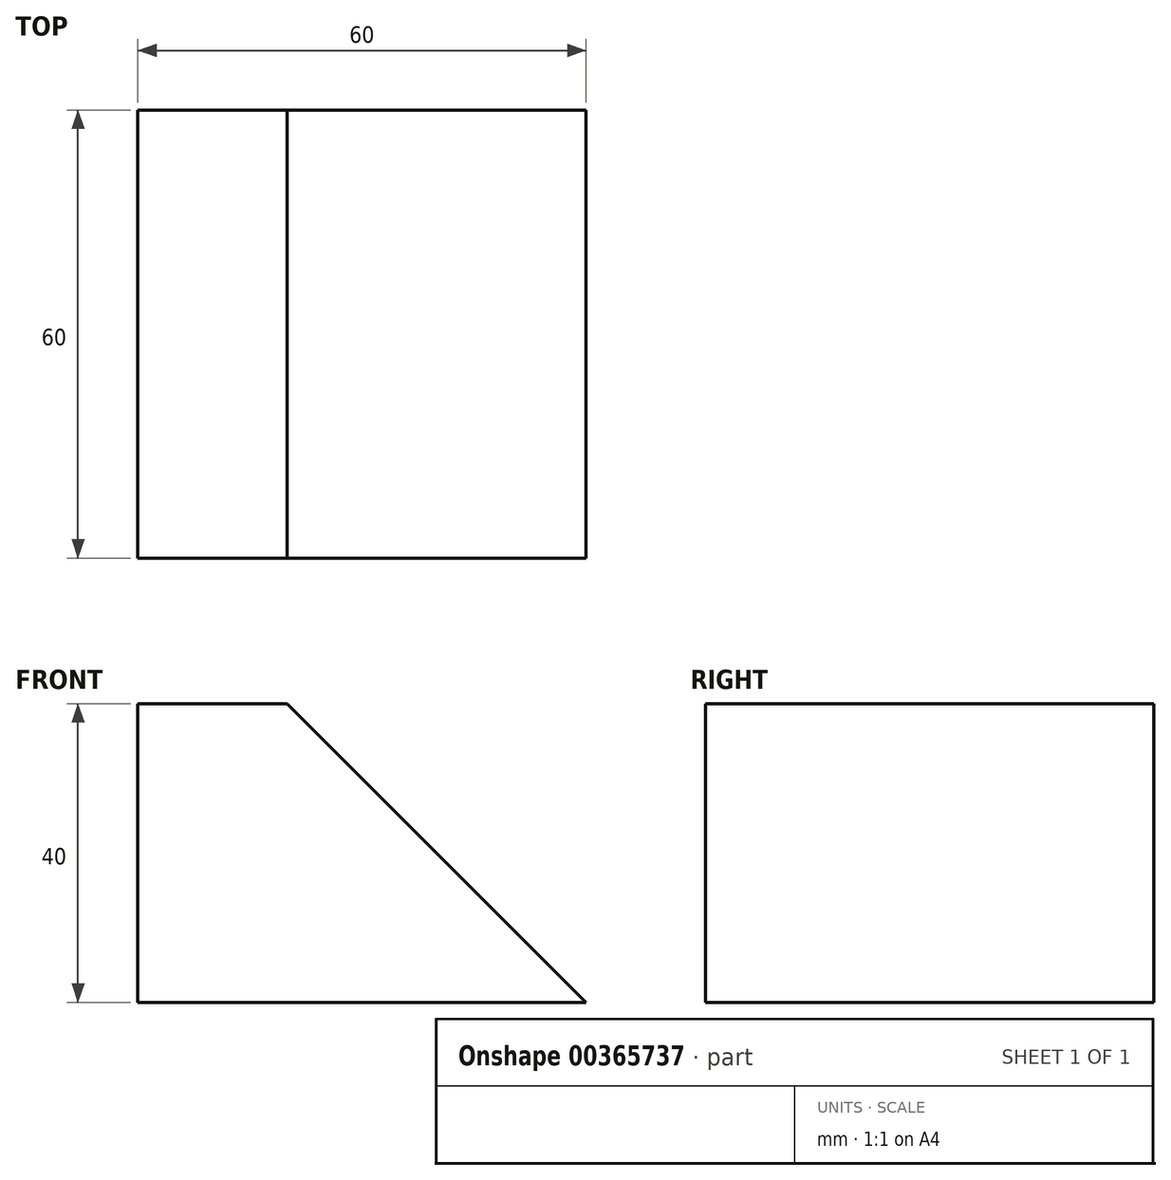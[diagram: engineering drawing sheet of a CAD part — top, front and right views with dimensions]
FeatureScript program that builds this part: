
annotation { "Feature Type Name" : "Feature", "Feature Type Description" : "" }
export const myFeature = defineFeature(function(context is Context, id is Id, definition is map)
    precondition{}
    {
        {
            var Q0;
            Q0=qCreatedBy(makeId("Front.planeOp"),FACE);
            var sketch = newSketch(context, id + "F0", { "sketchPlane" : qUnion([Q0])});
            skLineSegment(sketch, "E0", {"start": v(0, 0) * mm, "end": v(-40, 40) * mm});
            skLineSegment(sketch, "E1", {"start": v(-40, 40) * mm, "end": v(-60, 40) * mm});
            skLineSegment(sketch, "E2", {"start": v(-60, 40) * mm, "end": v(-60, 0) * mm});
            skLineSegment(sketch, "E3", {"start": v(-60, 0) * mm, "end": v(0, 0) * mm});
            skSolve(sketch);
        }
        {
            var Q0;
            Q0=makeQuery(id+"F0.imprint","IMPRINT",FACE,{"disambiguationData":[TD([[makeQuery(id+"F0.imprint","IMPRINT",EDGE,{"derivedFrom":sQuery(id+"F0.wireOp",EDGE,"E0")}),1.0]])]});
            extrude(context, id + "F1", {"entities" : qUnion([Q0]), "endBound" : BoundingType.SYMMETRIC, "depth" : 60 * mm});
        }
        {
            var Q0;
            Q0=qCreatedBy(makeId("Front.planeOp"),FACE);
            var sketch = newSketch(context, id + "F2", { "sketchPlane" : qUnion([Q0])});
            skPoint(sketch, "E4", {"position": v(-20, 30) * mm});
            skSolve(sketch);
        }
        {
            var Q0;
            Q0=makeQuery(id+"F1.opExtrude","SWEPT_FACE",FACE,{"disambiguationData":[OSD([sQuery(id+"F0.wireOp",EDGE,"E0")])]});
            var sketch = newSketch(context, id + "F3", { "sketchPlane" : qUnion([Q0])});
            skPoint(sketch, "E5", {"position": v(0, 56.57) * mm});
            skSolve(sketch);
        }
    });
